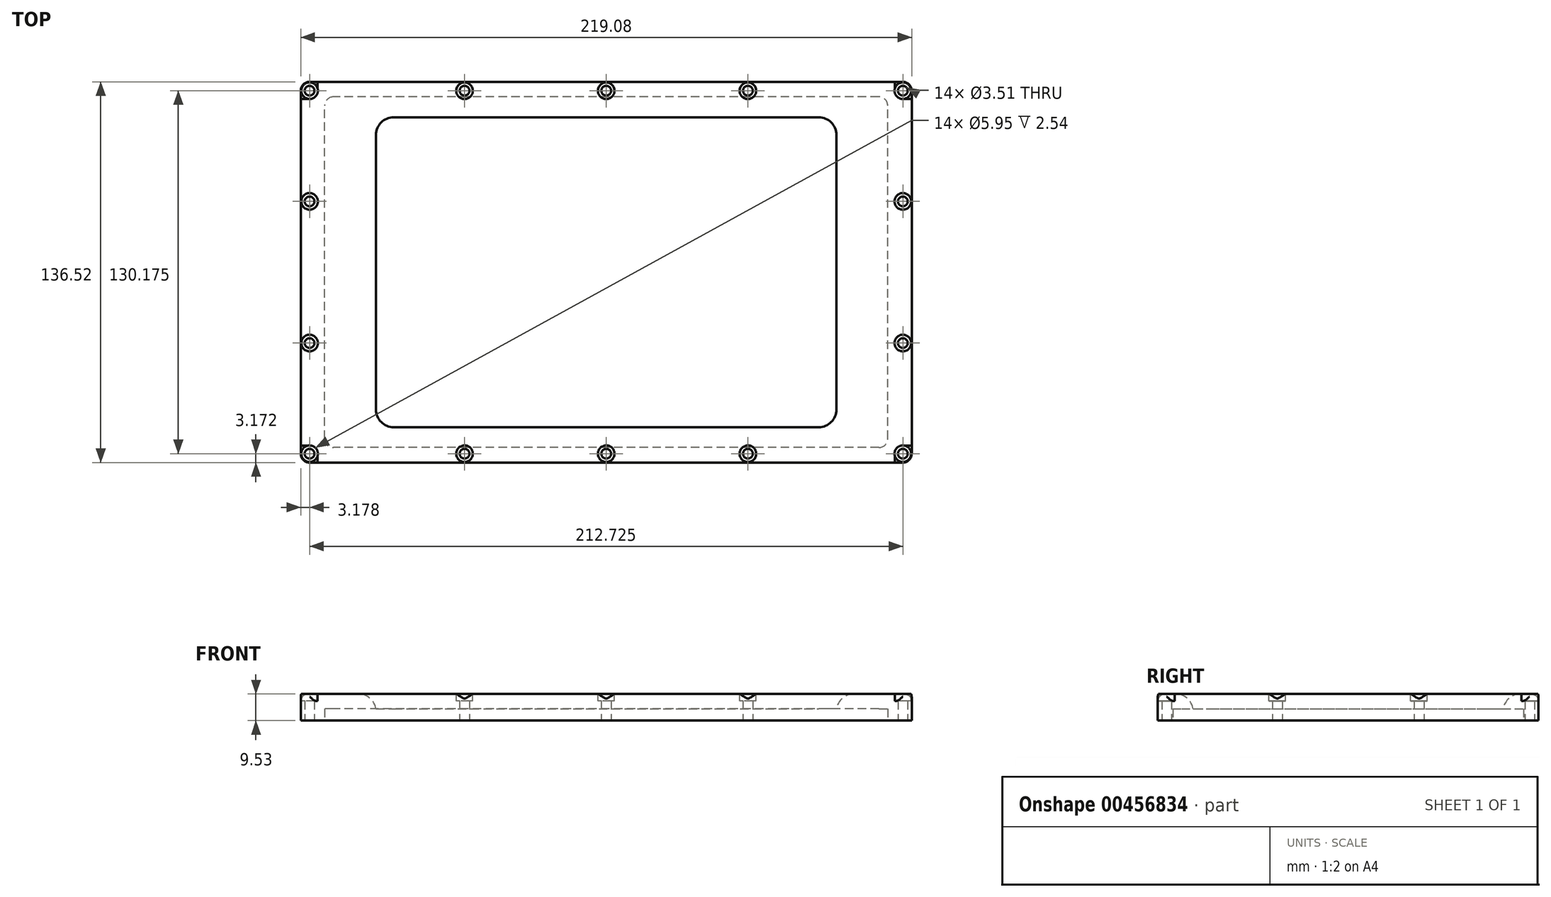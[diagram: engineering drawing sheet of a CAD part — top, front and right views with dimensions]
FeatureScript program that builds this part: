
annotation { "Feature Type Name" : "Feature", "Feature Type Description" : "" }
export const myFeature = defineFeature(function(context is Context, id is Id, definition is map)
    precondition{}
    {
        {
            var Q0;
            Q0=qCreatedBy(makeId("Top.planeOp"),FACE);
            var sketch = newSketch(context, id + "F0", { "sketchPlane" : qUnion([Q0])});
            skLineSegment(sketch, "E0.bottom", {"start": v(76.2, 49.21) * mm, "end": v(-76.2, 49.21) * mm, "construction": true});
            skLineSegment(sketch, "E0.top", {"start": v(76.2, -49.21) * mm, "end": v(-76.2, -49.21) * mm, "construction": true});
            skLineSegment(sketch, "E0.left", {"start": v(76.2, 49.21) * mm, "end": v(76.2, -49.21) * mm, "construction": true});
            skLineSegment(sketch, "E0.right", {"start": v(-76.2, 49.21) * mm, "end": v(-76.2, -49.21) * mm, "construction": true});
            skPoint(sketch, "E0.middle", {"position": v(0, 0) * mm});
            skLineSegment(sketch, "E1.bottom", {"start": v(76.2, 55.56) * mm, "end": v(-76.2, 55.56) * mm});
            skLineSegment(sketch, "E1.top", {"start": v(76.2, -55.56) * mm, "end": v(-76.2, -55.56) * mm});
            skLineSegment(sketch, "E1.left", {"start": v(82.55, 49.21) * mm, "end": v(82.55, -49.21) * mm});
            skLineSegment(sketch, "E1.right", {"start": v(-82.55, 49.21) * mm, "end": v(-82.55, -49.21) * mm});
            skPoint(sketch, "E2.visualSharp", {"position": v(-82.55, 55.56) * mm});
            skArc(sketch, "E2.filletArc", {"start": v(-76.2, 55.56) * mm, "mid": v(-80.7, 53.7) * mm, "end": v(-82.55, 49.21) * mm});
            skPoint(sketch, "E3.visualSharp", {"position": v(82.55, 55.56) * mm});
            skArc(sketch, "E3.filletArc", {"start": v(82.55, 49.21) * mm, "mid": v(80.7, 53.7) * mm, "end": v(76.2, 55.56) * mm});
            skPoint(sketch, "E4.visualSharp", {"position": v(82.55, -55.56) * mm});
            skArc(sketch, "E4.filletArc", {"start": v(76.2, -55.56) * mm, "mid": v(80.7, -53.7) * mm, "end": v(82.55, -49.21) * mm});
            skPoint(sketch, "E5.visualSharp", {"position": v(-82.55, -55.56) * mm});
            skArc(sketch, "E5.filletArc", {"start": v(-82.55, -49.21) * mm, "mid": v(-80.7, -53.7) * mm, "end": v(-76.2, -55.56) * mm});
            skLineSegment(sketch, "E6.bottom", {"start": v(106.36, 68.26) * mm, "end": v(-106.36, 68.26) * mm});
            skLineSegment(sketch, "E6.top", {"start": v(106.36, -68.26) * mm, "end": v(-106.36, -68.26) * mm});
            skLineSegment(sketch, "E6.left", {"start": v(109.54, 65.09) * mm, "end": v(109.54, -65.09) * mm});
            skLineSegment(sketch, "E6.right", {"start": v(-109.54, 65.09) * mm, "end": v(-109.54, -65.09) * mm});
            skPoint(sketch, "E7.visualSharp", {"position": v(-109.54, 68.26) * mm});
            skArc(sketch, "E7.filletArc", {"start": v(-106.36, 68.26) * mm, "mid": v(-108.6, 67.33) * mm, "end": v(-109.54, 65.09) * mm});
            skPoint(sketch, "E8.visualSharp", {"position": v(109.54, 68.26) * mm});
            skArc(sketch, "E8.filletArc", {"start": v(109.54, 65.09) * mm, "mid": v(108.6, 67.33) * mm, "end": v(106.36, 68.26) * mm});
            skPoint(sketch, "E9.visualSharp", {"position": v(109.54, -68.26) * mm});
            skArc(sketch, "E9.filletArc", {"start": v(106.36, -68.26) * mm, "mid": v(108.6, -67.33) * mm, "end": v(109.54, -65.09) * mm});
            skPoint(sketch, "E10.visualSharp", {"position": v(-109.54, -68.26) * mm});
            skArc(sketch, "E10.filletArc", {"start": v(-109.54, -65.09) * mm, "mid": v(-108.6, -67.33) * mm, "end": v(-106.36, -68.26) * mm});
            skSolve(sketch);
        }
        {
            var Q0;
            Q0 = qSketchRegion(id + "F0", true);
            extrude(context, id + "F1", {"entities" : qUnion([Q0]), "depth" : 9.52 * mm});
        }
        {
            var Q0;
            Q0=makeQuery(id+"F1.opExtrude","CAP_FACE",FACE,{"disambiguationData":[OSD([sQuery(id+"F0.wireOp",EDGE,"E1.bottom"),sQuery(id+"F0.wireOp",EDGE,"E1.top"),sQuery(id+"F0.wireOp",EDGE,"E1.left"),sQuery(id+"F0.wireOp",EDGE,"E1.right"),sQuery(id+"F0.wireOp",EDGE,"E2.filletArc"),sQuery(id+"F0.wireOp",EDGE,"E3.filletArc"),sQuery(id+"F0.wireOp",EDGE,"E4.filletArc"),sQuery(id+"F0.wireOp",EDGE,"E5.filletArc"),sQuery(id+"F0.wireOp",EDGE,"E6.bottom"),sQuery(id+"F0.wireOp",EDGE,"E6.top"),sQuery(id+"F0.wireOp",EDGE,"E6.left"),sQuery(id+"F0.wireOp",EDGE,"E6.right"),sQuery(id+"F0.wireOp",EDGE,"E7.filletArc"),sQuery(id+"F0.wireOp",EDGE,"E8.filletArc"),sQuery(id+"F0.wireOp",EDGE,"E9.filletArc"),sQuery(id+"F0.wireOp",EDGE,"E10.filletArc")])],"isStart":true});
            var sketch = newSketch(context, id + "F2", { "sketchPlane" : qUnion([Q0])});
            skLineSegment(sketch, "E11.bottom", {"start": v(97.8, 62.87) * mm, "end": v(-97.8, 62.87) * mm});
            skLineSegment(sketch, "E11.top", {"start": v(97.8, -62.86) * mm, "end": v(-97.8, -62.86) * mm});
            skLineSegment(sketch, "E11.left", {"start": v(100.97, 59.7) * mm, "end": v(100.97, -59.69) * mm});
            skLineSegment(sketch, "E11.right", {"start": v(-100.97, 59.7) * mm, "end": v(-100.97, -59.69) * mm});
            skPoint(sketch, "E11.middle", {"position": v(0, 0) * mm});
            skPoint(sketch, "E12.visualSharp", {"position": v(-100.97, 62.87) * mm});
            skArc(sketch, "E12.filletArc", {"start": v(-97.8, 62.87) * mm, "mid": v(-100.04, 61.94) * mm, "end": v(-100.97, 59.7) * mm});
            skPoint(sketch, "E13.visualSharp", {"position": v(-100.97, -62.86) * mm});
            skArc(sketch, "E13.filletArc", {"start": v(-100.97, -59.69) * mm, "mid": v(-100.04, -61.94) * mm, "end": v(-97.8, -62.86) * mm});
            skPoint(sketch, "E14.visualSharp", {"position": v(100.97, 62.87) * mm});
            skArc(sketch, "E14.filletArc", {"start": v(100.97, 59.7) * mm, "mid": v(100.04, 61.94) * mm, "end": v(97.8, 62.87) * mm});
            skPoint(sketch, "E15.visualSharp", {"position": v(100.97, -62.86) * mm});
            skArc(sketch, "E15.filletArc", {"start": v(97.8, -62.86) * mm, "mid": v(100.04, -61.94) * mm, "end": v(100.97, -59.69) * mm});
            skSolve(sketch);
        }
        {
            var Q0;
            Q0 = qSketchRegion(id + "F2", true);
            extrude(context, id + "F3", {"entities" : qUnion([Q0]), "operationType" : NewBodyOperationType.REMOVE, "oppositeDirection" : true, "depth" : 4.2 * mm});
        }
        {
            var Q0;
            Q0=makeQuery(id+"F1.opExtrude","CAP_FACE",FACE,{"disambiguationData":[OSD([sQuery(id+"F0.wireOp",EDGE,"E1.bottom"),sQuery(id+"F0.wireOp",EDGE,"E1.top"),sQuery(id+"F0.wireOp",EDGE,"E1.left"),sQuery(id+"F0.wireOp",EDGE,"E1.right"),sQuery(id+"F0.wireOp",EDGE,"E2.filletArc"),sQuery(id+"F0.wireOp",EDGE,"E3.filletArc"),sQuery(id+"F0.wireOp",EDGE,"E4.filletArc"),sQuery(id+"F0.wireOp",EDGE,"E5.filletArc"),sQuery(id+"F0.wireOp",EDGE,"E6.bottom"),sQuery(id+"F0.wireOp",EDGE,"E6.top"),sQuery(id+"F0.wireOp",EDGE,"E6.left"),sQuery(id+"F0.wireOp",EDGE,"E6.right"),sQuery(id+"F0.wireOp",EDGE,"E7.filletArc"),sQuery(id+"F0.wireOp",EDGE,"E8.filletArc"),sQuery(id+"F0.wireOp",EDGE,"E9.filletArc"),sQuery(id+"F0.wireOp",EDGE,"E10.filletArc")])],"isStart":true});
            var sketch = newSketch(context, id + "F4", { "sketchPlane" : qUnion([Q0])});
            skPoint(sketch, "E16", {"position": v(0, -65.09) * mm});
            skPoint(sketch, "E16.positionSnap0", {"position": v(0, -62.87) * mm});
            skPoint(sketch, "E17", {"position": v(-50.8, -65.09) * mm});
            skPoint(sketch, "E18", {"position": v(-106.36, -65.09) * mm});
            skPoint(sketch, "E19", {"position": v(-106.36, -25.4) * mm});
            skPoint(sketch, "E20", {"position": v(-106.36, 25.4) * mm});
            skPoint(sketch, "E21", {"position": v(-106.36, 65.09) * mm});
            skPoint(sketch, "E22", {"position": v(-50.8, 65.09) * mm});
            skPoint(sketch, "E23", {"position": v(0, 65.09) * mm});
            skPoint(sketch, "E24", {"position": v(50.8, 65.09) * mm});
            skPoint(sketch, "E25", {"position": v(106.36, 65.09) * mm});
            skPoint(sketch, "E26", {"position": v(106.36, 25.4) * mm});
            skPoint(sketch, "E27", {"position": v(106.36, -25.4) * mm});
            skPoint(sketch, "E28", {"position": v(106.36, -65.09) * mm});
            skPoint(sketch, "E29", {"position": v(50.8, -65.09) * mm});
            skLineSegment(sketch, "E30.bottom", {"start": v(-106.36, -65.09) * mm, "end": v(106.36, -65.09) * mm});
            skLineSegment(sketch, "E30.top", {"start": v(-106.36, 65.09) * mm, "end": v(106.36, 65.09) * mm});
            skLineSegment(sketch, "E30.left", {"start": v(-106.36, -65.09) * mm, "end": v(-106.36, 65.09) * mm});
            skLineSegment(sketch, "E30.right", {"start": v(106.36, -65.09) * mm, "end": v(106.36, 65.09) * mm});
            skPoint(sketch, "E30.middle", {"position": v(0, 0) * mm});
            skLineSegment(sketch, "E31", {"start": v(-103.19, 0) * mm, "end": v(-109.54, 0) * mm, "construction": true});
            skPoint(sketch, "E32", {"position": v(-106.36, 0) * mm});
            skLineSegment(sketch, "E33", {"start": v(0, -62.87) * mm, "end": v(0, -68.26) * mm, "construction": true});
            skSolve(sketch);
        }
        {
            var Q0;
            Q0=sQuery(id+"F4.wireOp",VERTEX,"E24");
            var Q1;
            Q1=sQuery(id+"F4.wireOp",VERTEX,"E23");
            var Q2;
            Q2=sQuery(id+"F4.wireOp",VERTEX,"E22");
            var Q3;
            Q3=sQuery(id+"F4.wireOp",VERTEX,"E26");
            var Q4;
            Q4=sQuery(id+"F4.wireOp",VERTEX,"E27");
            var Q5;
            Q5=sQuery(id+"F4.wireOp",VERTEX,"E29");
            var Q6;
            Q6=sQuery(id+"F4.wireOp",VERTEX,"E16");
            var Q7;
            Q7=sQuery(id+"F4.wireOp",VERTEX,"E17");
            var Q8;
            Q8=sQuery(id+"F4.wireOp",VERTEX,"E20");
            var Q9;
            Q9=sQuery(id+"F4.wireOp",VERTEX,"E19");
            var Q10;
            Q10=sQuery(id+"F4.wireOp",VERTEX,"E18");
            var Q11;
            Q11=sQuery(id+"F4.wireOp",VERTEX,"E21");
            var Q12;
            Q12=sQuery(id+"F4.wireOp",VERTEX,"E28");
            var Q13;
            Q13=sQuery(id+"F4.wireOp",VERTEX,"E25");
            var Q14;
            Q14=makeQuery(id+"F1.opExtrude","SWEPT_BODY",BODY,{"disambiguationData":[OSD([sQuery(id+"F0.wireOp",EDGE,"E1.bottom"),sQuery(id+"F0.wireOp",EDGE,"E1.top"),sQuery(id+"F0.wireOp",EDGE,"E1.left"),sQuery(id+"F0.wireOp",EDGE,"E1.right"),sQuery(id+"F0.wireOp",EDGE,"E2.filletArc"),sQuery(id+"F0.wireOp",EDGE,"E3.filletArc"),sQuery(id+"F0.wireOp",EDGE,"E4.filletArc"),sQuery(id+"F0.wireOp",EDGE,"E5.filletArc"),sQuery(id+"F0.wireOp",EDGE,"E6.bottom"),sQuery(id+"F0.wireOp",EDGE,"E6.top"),sQuery(id+"F0.wireOp",EDGE,"E6.left"),sQuery(id+"F0.wireOp",EDGE,"E6.right"),sQuery(id+"F0.wireOp",EDGE,"E7.filletArc"),sQuery(id+"F0.wireOp",EDGE,"E8.filletArc"),sQuery(id+"F0.wireOp",EDGE,"E9.filletArc"),sQuery(id+"F0.wireOp",EDGE,"E10.filletArc")])]});
            hole(context, id + "F5", {"style" : HoleStyle.SIMPLE, "endStyle" : HoleEndStyle.THROUGH, "holeDiameter" : 3.5 * mm, "isTappedThrough" : true, "tappedDepth" : 12.7 * mm, "tapClearance" : 3, "locations" : qUnion([Q0, Q1, Q2, Q3, Q4, Q5, Q6, Q7, Q8, Q9, Q10, Q11, Q12, Q13]), "scope" : qUnion([Q14])});
        }
        {
            var Q0;
            Q0=makeQuery(id+"F1.opExtrude","CAP_FACE",FACE,{"disambiguationData":[OSD([sQuery(id+"F0.wireOp",EDGE,"E1.bottom"),sQuery(id+"F0.wireOp",EDGE,"E1.top"),sQuery(id+"F0.wireOp",EDGE,"E1.left"),sQuery(id+"F0.wireOp",EDGE,"E1.right"),sQuery(id+"F0.wireOp",EDGE,"E2.filletArc"),sQuery(id+"F0.wireOp",EDGE,"E3.filletArc"),sQuery(id+"F0.wireOp",EDGE,"E4.filletArc"),sQuery(id+"F0.wireOp",EDGE,"E5.filletArc"),sQuery(id+"F0.wireOp",EDGE,"E6.bottom"),sQuery(id+"F0.wireOp",EDGE,"E6.top"),sQuery(id+"F0.wireOp",EDGE,"E6.left"),sQuery(id+"F0.wireOp",EDGE,"E6.right"),sQuery(id+"F0.wireOp",EDGE,"E7.filletArc"),sQuery(id+"F0.wireOp",EDGE,"E8.filletArc"),sQuery(id+"F0.wireOp",EDGE,"E9.filletArc"),sQuery(id+"F0.wireOp",EDGE,"E10.filletArc")])],"isStart":false});
            var sketch = newSketch(context, id + "F6", { "sketchPlane" : qUnion([Q0])});
            skCircle(sketch, "E34", {"center": v(-106.36, 65.09) * mm, "radius": 2.98 * mm});
            skCircle(sketch, "E35", {"center": v(-50.8, 65.09) * mm, "radius": 2.98 * mm});
            skCircle(sketch, "E36", {"center": v(0, 65.09) * mm, "radius": 2.98 * mm});
            skCircle(sketch, "E37", {"center": v(50.8, 65.09) * mm, "radius": 2.98 * mm});
            skCircle(sketch, "E38", {"center": v(106.36, 65.09) * mm, "radius": 2.98 * mm});
            skCircle(sketch, "E39", {"center": v(106.36, 25.4) * mm, "radius": 2.98 * mm});
            skCircle(sketch, "E40", {"center": v(106.36, -25.4) * mm, "radius": 2.98 * mm});
            skCircle(sketch, "E41", {"center": v(106.36, -65.09) * mm, "radius": 2.98 * mm});
            skCircle(sketch, "E42", {"center": v(50.8, -65.09) * mm, "radius": 2.98 * mm});
            skCircle(sketch, "E43", {"center": v(0, -65.09) * mm, "radius": 2.98 * mm});
            skCircle(sketch, "E44", {"center": v(-50.8, -65.09) * mm, "radius": 2.98 * mm});
            skCircle(sketch, "E45", {"center": v(-106.36, -65.09) * mm, "radius": 2.98 * mm});
            skCircle(sketch, "E46", {"center": v(-106.36, -25.4) * mm, "radius": 2.98 * mm});
            skCircle(sketch, "E47", {"center": v(-106.36, 25.4) * mm, "radius": 2.98 * mm});
            skSolve(sketch);
        }
        {
            var Q0;
            Q0 = qSketchRegion(id + "F6", true);
            extrude(context, id + "F7", {"entities" : qUnion([Q0]), "operationType" : NewBodyOperationType.REMOVE, "oppositeDirection" : true, "depth" : 2.54 * mm});
        }
        {
            var Q0;
            Q0=makeQuery(id+"F1.opExtrude","CAP_EDGE",EDGE,{"disambiguationData":[OSD([sQuery(id+"F0.wireOp",EDGE,"E1.right")])],"isStart":false});
            fillet(context, id + "F8", {"entities" : qUnion([Q0]), "radius" : 6.35 * mm, "tangentPropagation" : true, "allowEdgeOverflow" : false});
        }
        {
            var Q0;
            Q0=makeQuery(id+"F1.opExtrude","CAP_EDGE",EDGE,{"disambiguationData":[OSD([sQuery(id+"F0.wireOp",EDGE,"E6.right")])],"isStart":false});
            fillet(context, id + "F9", {"entities" : qUnion([Q0]), "radius" : 2.54 * mm, "tangentPropagation" : true, "allowEdgeOverflow" : false});
        }
    });
